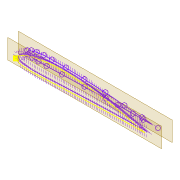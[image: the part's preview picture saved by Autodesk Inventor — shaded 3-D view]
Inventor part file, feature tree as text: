
AUTODESK INVENTOR PART (.ipt)
format: ipt  version: 2022 (Build 260153000, 153)  size: 127,488 bytes
history: native  units: mm
features: sketch x3, plane x2
ambient origin geometry x8: Origin, YZ Plane, XZ Plane, XY Plane, X Axis, Y Axis, Z Axis, Center Point
feature tree (5):
  sketch  "Sketch15"  dims[d33=5.0mm]
  plane  "Work Plane2"
  sketch  "Sketch17"  dims[d34=-20.0mm]
  plane  "Work Plane3"
  sketch  "Sketch19"
